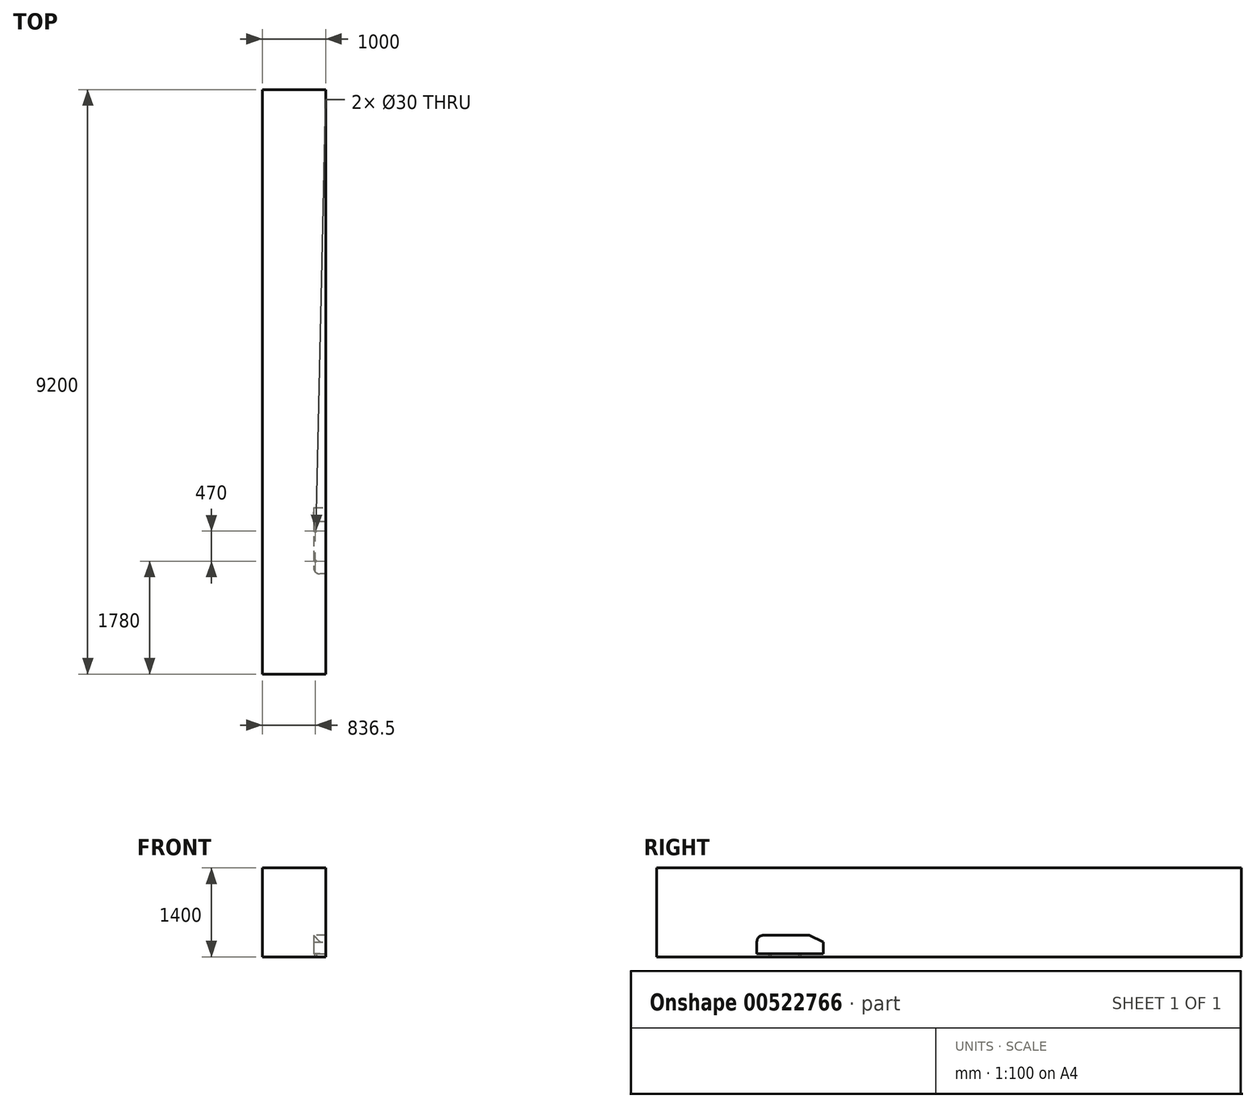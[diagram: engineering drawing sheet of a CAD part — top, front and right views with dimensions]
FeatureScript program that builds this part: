
annotation { "Feature Type Name" : "Feature", "Feature Type Description" : "" }
export const myFeature = defineFeature(function(context is Context, id is Id, definition is map)
    precondition{}
    {
        {
            var Q0;
            Q0=qCreatedBy(makeId("Top.planeOp"),FACE);
            var sketch = newSketch(context, id + "F0", { "sketchPlane" : qUnion([Q0])});
            skLineSegment(sketch, "E0.bottom", {"start": v(192, 522) * mm, "end": v(-192, 522) * mm});
            skLineSegment(sketch, "E0.top", {"start": v(192, -522) * mm, "end": v(-192, -522) * mm});
            skLineSegment(sketch, "E0.left", {"start": v(192, 522) * mm, "end": v(192, -522) * mm});
            skLineSegment(sketch, "E0.right", {"start": v(-192, 522) * mm, "end": v(-192, -522) * mm});
            skPoint(sketch, "E0.middle", {"position": v(0, 0) * mm});
            skSolve(sketch);
        }
        {
            var Q0;
            Q0=qSketchRegion(id+"F0",true);
            extrude(context, id + "F1", {"entities" : qUnion([Q0]), "depth" : 338 * mm});
        }
        {
            var Q0;
            Q0=makeQuery(id+"F1.opExtrude","SWEPT_FACE",FACE,{"disambiguationData":[OSD([sQuery(id+"F0.wireOp",EDGE,"E0.top")])]});
            var sketch = newSketch(context, id + "F2", { "sketchPlane" : qUnion([Q0])});
            skLineSegment(sketch, "E1.bottom", {"start": v(-192, 0) * mm, "end": v(192, 0) * mm});
            skLineSegment(sketch, "E1.top", {"start": v(-192, 50) * mm, "end": v(192, 50) * mm});
            skLineSegment(sketch, "E1.left", {"start": v(-192, 0) * mm, "end": v(-192, 50) * mm});
            skLineSegment(sketch, "E1.right", {"start": v(192, 0) * mm, "end": v(192, 50) * mm});
            skSolve(sketch);
        }
        {
            var Q0;
            Q0=qSketchRegion(id+"F2",true);
            extrude(context, id + "F3", {"entities" : qUnion([Q0]), "operationType" : NewBodyOperationType.REMOVE, "endBound" : BoundingType.THROUGH_ALL, "oppositeDirection" : true, "depth" : 25 * mm});
        }
        {
            var Q0;
            Q0=makeQuery(id+"F1.opExtrude","SWEPT_EDGE",EDGE,{"disambiguationData":[OSD([sQuery(id+"F0.wireOp",EDGE,"E0.top"),sQuery(id+"F0.wireOp",EDGE,"E0.right")])]});
            var Q1;
            Q1=makeQuery(id+"F1.opExtrude","CAP_EDGE",EDGE,{"disambiguationData":[OSD([sQuery(id+"F0.wireOp",EDGE,"E0.top")])],"isStart":false});
            var Q2;
            Q2=makeQuery(id+"F1.opExtrude","SWEPT_EDGE",EDGE,{"disambiguationData":[OSD([sQuery(id+"F0.wireOp",EDGE,"E0.top"),sQuery(id+"F0.wireOp",EDGE,"E0.left")])]});
            var Q3;
            Q3=makeQuery(id+"F3.boolean.opBoolean","COPY",EDGE,{"derivedFrom":makeQuery(id+"F3.opExtrude","CAP_EDGE",EDGE,{"disambiguationData":[OSD([sQuery(id+"F2.wireOp",EDGE,"E1.top")])],"isStart":true})});
            fillet(context, id + "F4", {"entities" : qUnion([Q0, Q1, Q2, Q3]), "radius" : 100 * mm, "tangentPropagation" : true, "allowEdgeOverflow" : false});
        }
        {
            var Q0;
            Q0=makeQuery(id+"F1.opExtrude","CAP_EDGE",EDGE,{"disambiguationData":[OSD([sQuery(id+"F0.wireOp",EDGE,"E0.bottom")])],"isStart":false});
            chamfer(context, id + "F5", {"entities" : qUnion([Q0]), "chamferType" : ChamferType.OFFSET_ANGLE, "width" : 222 * mm, "oppositeDirection" : false, "angle" : 25 * degree, "tangentPropagation" : true});
        }
        {
            var Q0;
            Q0=qCreatedBy(makeId("Top.planeOp"),FACE);
            var sketch = newSketch(context, id + "F6", { "sketchPlane" : qUnion([Q0])});
            skCircle(sketch, "E2", {"center": v(163.5, -320) * mm, "radius": 15 * mm});
            skCircle(sketch, "E3", {"center": v(163.5, 150) * mm, "radius": 15 * mm});
            skCircle(sketch, "E4", {"center": v(-163.5, 150) * mm, "radius": 15 * mm});
            skCircle(sketch, "E5", {"center": v(-163.5, -320) * mm, "radius": 15 * mm});
            skSolve(sketch);
        }
        {
            var Q0;
            Q0=qSketchRegion(id+"F6",true);
            extrude(context, id + "F7", {"entities" : qUnion([Q0]), "operationType" : NewBodyOperationType.ADD, "endBound" : BoundingType.UP_TO_NEXT, "depth" : 25 * mm});
        }
        {
            var Q0;
            Q0=qCreatedBy(makeId("Top.planeOp"),FACE);
            var sketch = newSketch(context, id + "F8", { "sketchPlane" : qUnion([Q0])});
            skLineSegment(sketch, "E6.bottom", {"start": v(-1000, 7100) * mm, "end": v(1000, 7100) * mm});
            skLineSegment(sketch, "E6.top", {"start": v(-1000, -2100) * mm, "end": v(1000, -2100) * mm});
            skLineSegment(sketch, "E6.left", {"start": v(-1000, 7100) * mm, "end": v(-1000, -2100) * mm});
            skLineSegment(sketch, "E6.right", {"start": v(1000, 7100) * mm, "end": v(1000, -2100) * mm});
            skSolve(sketch);
        }
        {
            var Q0;
            Q0=qSketchRegion(id+"F8",true);
            extrude(context, id + "F9", {"entities" : qUnion([Q0]), "depth" : 1400 * mm});
        }
        {
            var Q0;
            Q0=makeQuery(id+"F1.opExtrude","SWEPT_BODY",BODY,{"disambiguationData":[OSD([sQuery(id+"F0.wireOp",EDGE,"E0.bottom"),sQuery(id+"F0.wireOp",EDGE,"E0.top"),sQuery(id+"F0.wireOp",EDGE,"E0.left"),sQuery(id+"F0.wireOp",EDGE,"E0.right")])]});
            var Q1;
            Q1=makeQuery(id+"F9.opExtrude","SWEPT_BODY",BODY,{"disambiguationData":[OSD([sQuery(id+"F8.wireOp",EDGE,"E6.bottom"),sQuery(id+"F8.wireOp",EDGE,"E6.top"),sQuery(id+"F8.wireOp",EDGE,"E6.left"),sQuery(id+"F8.wireOp",EDGE,"E6.right")])]});
            booleanBodies(context, id + "F10", {"operationType" : BooleanOperationType.SUBTRACTION, "tools" : qUnion([Q0]), "targets" : qUnion([Q1])});
        }
        {
            var Q0;
            Q0=makeQuery(id+"F9.opExtrude","SWEPT_FACE",FACE,{"disambiguationData":[OSD([sQuery(id+"F8.wireOp",EDGE,"E6.top")])]});
            var sketch = newSketch(context, id + "F11", { "sketchPlane" : qUnion([Q0])});
            skLineSegment(sketch, "E7.bottom", {"start": v(1000, 1400) * mm, "end": v(0, 1400) * mm});
            skLineSegment(sketch, "E7.top", {"start": v(1000, 0) * mm, "end": v(0, 0) * mm});
            skLineSegment(sketch, "E7.left", {"start": v(1000, 1400) * mm, "end": v(1000, 0) * mm});
            skLineSegment(sketch, "E7.right", {"start": v(0, 1400) * mm, "end": v(0, 0) * mm});
            skSolve(sketch);
        }
        {
            var Q0;
            Q0=makeQuery(id+"F11.imprint","IMPRINT",FACE,{"disambiguationData":[TD([[makeQuery(id+"F11.imprint","IMPRINT",EDGE,{"derivedFrom":sQuery(id+"F11.wireOp",EDGE,"E7.bottom")}),-1.0]])]});
            extrude(context, id + "F12", {"entities" : qUnion([Q0]), "operationType" : NewBodyOperationType.REMOVE, "endBound" : BoundingType.THROUGH_ALL, "oppositeDirection" : true, "depth" : 25 * mm});
        }
    });
